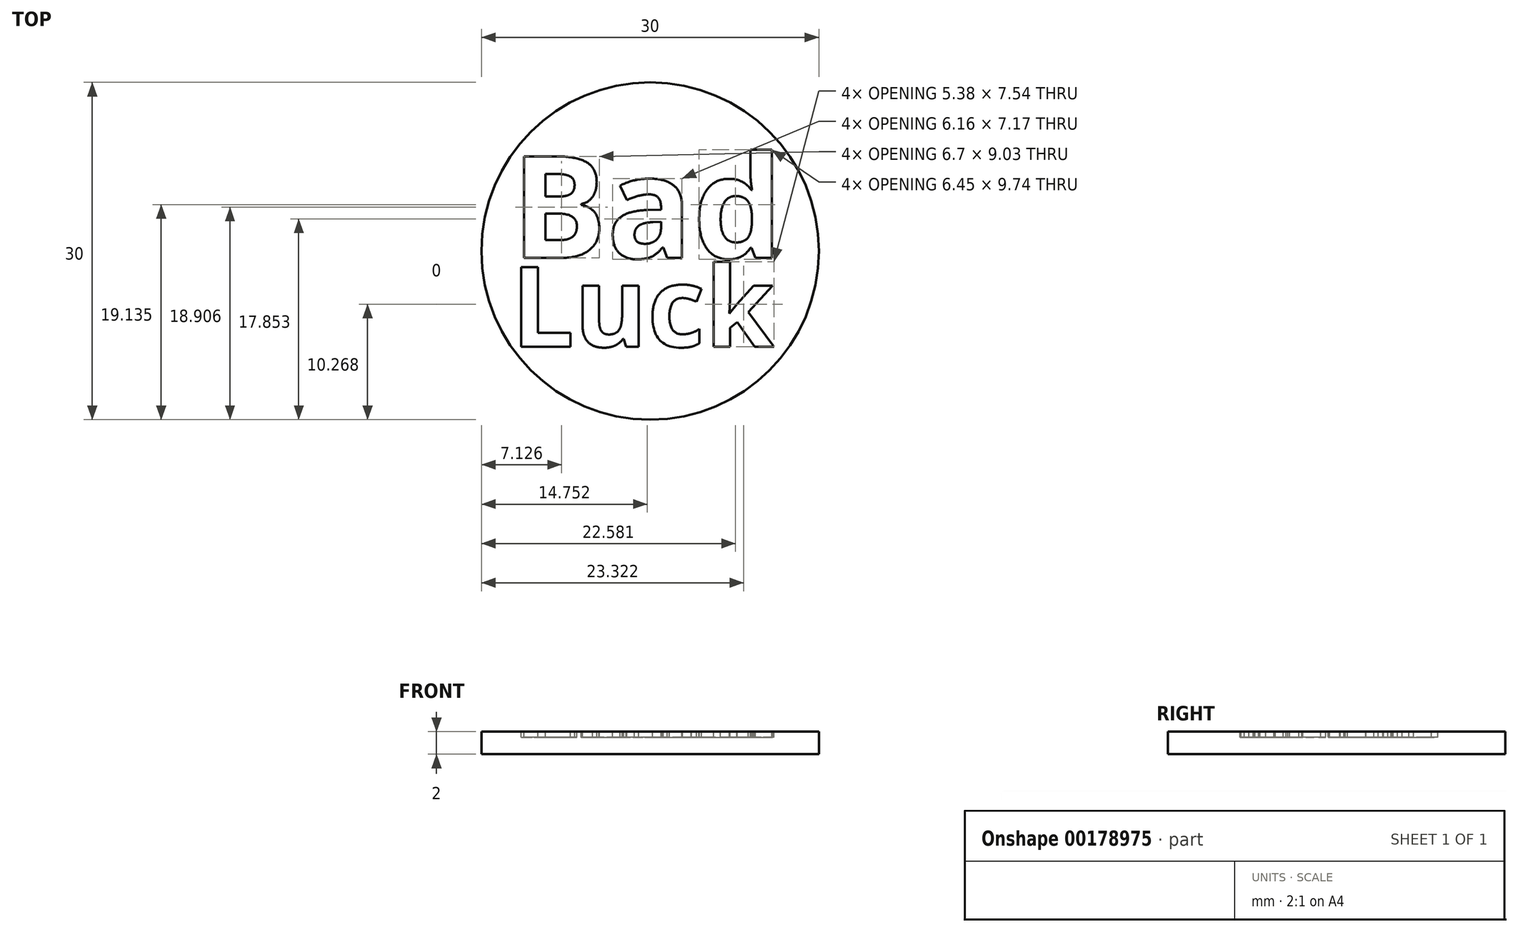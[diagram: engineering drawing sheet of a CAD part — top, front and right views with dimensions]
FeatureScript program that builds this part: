
annotation { "Feature Type Name" : "Feature", "Feature Type Description" : "" }
export const myFeature = defineFeature(function(context is Context, id is Id, definition is map)
    precondition{}
    {
        {
            var Q0;
            Q0=qCreatedBy(makeId("Top.planeOp"),FACE);
            var sketch = newSketch(context, id + "F0", { "sketchPlane" : qUnion([Q0])});
            skCircle(sketch, "E0", {"center": v(0, 0) * mm, "radius": 15 * mm});
            skSolve(sketch);
        }
        {
            var Q0;
            Q0 = qSketchRegion(id + "F0", true);
            extrude(context, id + "F1", {"entities" : qUnion([Q0]), "depth" : 2 * mm});
        }
        {
            var Q0;
            Q0=makeQuery(id+"F1.opExtrude","CAP_FACE",FACE,{"disambiguationData":[OSD([sQuery(id+"F0.wireOp",EDGE,"E0")])],"isStart":false});
            var sketch = newSketch(context, id + "F2", { "sketchPlane" : qUnion([Q0])});
            skLineSegment(sketch, "E1", {"start": v(-12.36, 8.5) * mm, "end": v(12.36, 8.5) * mm});
            skLineSegment(sketch, "E2", {"start": v(-12.36, 8.5) * mm, "end": v(-12.36, -8.5) * mm});
            skText(sketch, "E3", { "text": "Bad", "fontName": "OpenSans-Bold.ttf"});
            skText(sketch, "E4", { "text": "Luck", "fontName": "OpenSans-Bold.ttf"});
            const initialGuessF2  = {"E3": [-0.01236, -0.00061, 1, 0, 0.00911], "E4": [-0.01236, -0.0085, 1, 0, 0.00714]};
            skSetInitialGuess(sketch, initialGuessF2);
            skSolve(sketch);
        }
        {
            var Q0;
            Q0 = qSketchRegion(id + "F2", true);
            extrude(context, id + "F3", {"entities" : qUnion([Q0]), "operationType" : NewBodyOperationType.REMOVE, "oppositeDirection" : true, "depth" : 0.5 * mm});
        }
    });
